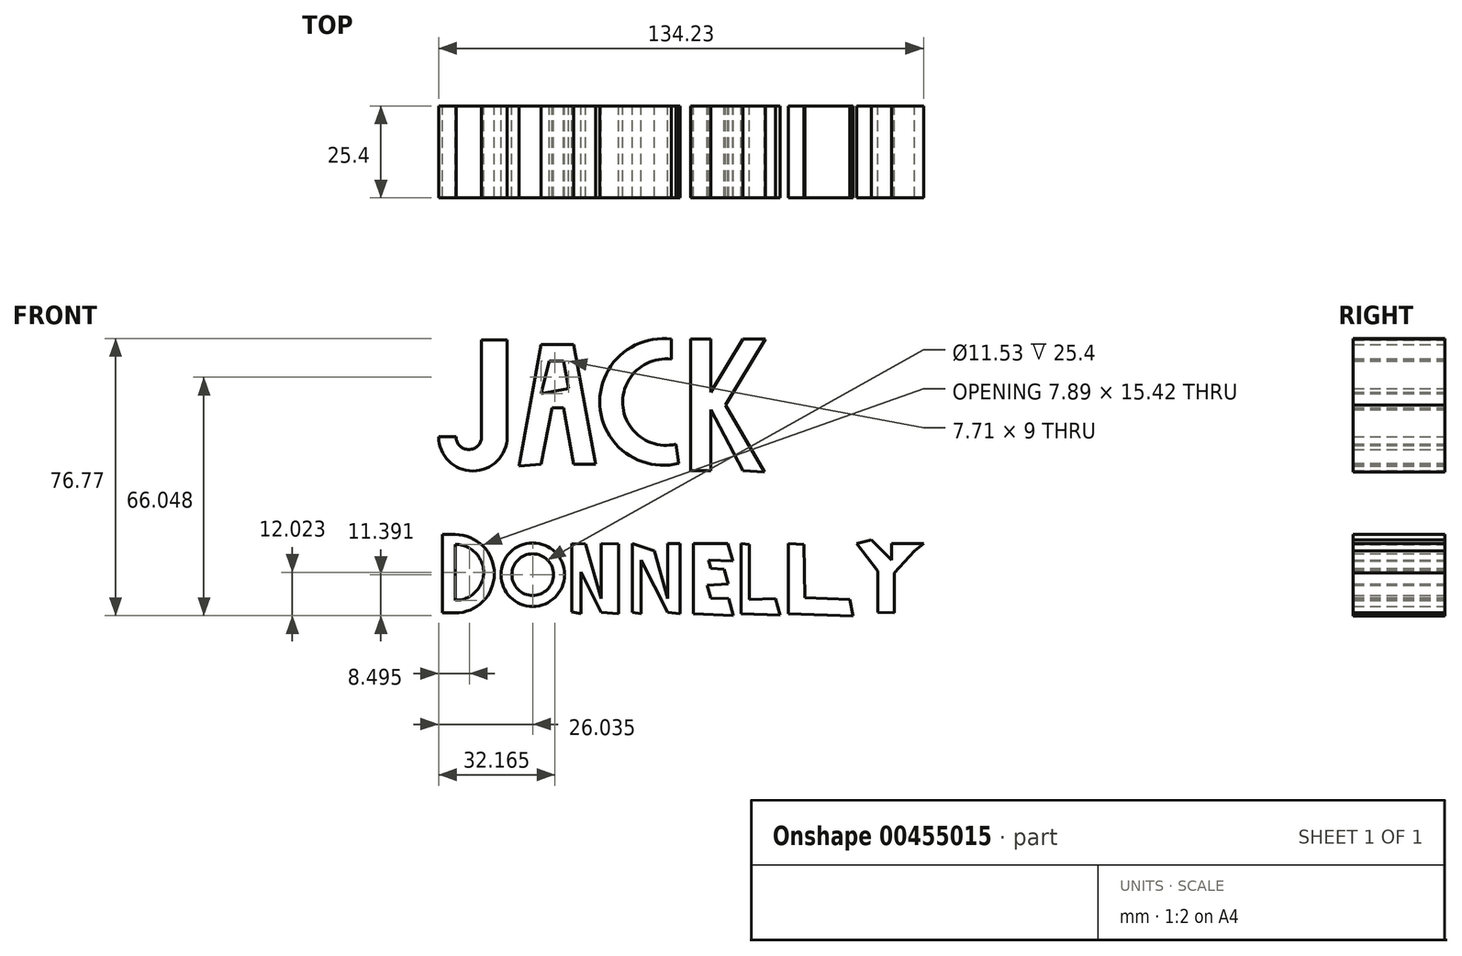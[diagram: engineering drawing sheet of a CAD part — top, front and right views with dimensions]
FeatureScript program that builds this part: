
annotation { "Feature Type Name" : "Feature", "Feature Type Description" : "" }
export const myFeature = defineFeature(function(context is Context, id is Id, definition is map)
    precondition{}
    {
        {
            var Q0;
            Q0=qCreatedBy(makeId("Front.planeOp"),FACE);
            var sketch = newSketch(context, id + "F0", { "sketchPlane" : qUnion([Q0])});
            skLineSegment(sketch, "E0", {"start": v(-63.45, 50.18) * mm, "end": v(-56.37, 50.18) * mm});
            skLineSegment(sketch, "E1", {"start": v(-56.37, 50.18) * mm, "end": v(-56.37, 23.38) * mm});
            skLineSegment(sketch, "E2", {"start": v(-63.45, 50.18) * mm, "end": v(-63.45, 23.38) * mm});
            skArc(sketch, "E3", {"start": v(-75.33, 23.38) * mm, "mid": v(-65.85, 13.9) * mm, "end": v(-56.37, 23.38) * mm});
            skLineSegment(sketch, "E4", {"start": v(-75.33, 23.38) * mm, "end": v(-70.53, 23.38) * mm});
            skArc(sketch, "E5", {"start": v(-70.53, 23.38) * mm, "mid": v(-67, 19.84) * mm, "end": v(-63.45, 23.38) * mm});
            skLineSegment(sketch, "E6", {"start": v(-53.09, 15.3) * mm, "end": v(-47.02, 48.92) * mm});
            skLineSegment(sketch, "E7", {"start": v(-47.02, 48.92) * mm, "end": v(-37.92, 48.92) * mm});
            skLineSegment(sketch, "E8", {"start": v(-37.92, 48.92) * mm, "end": v(-31.85, 15.8) * mm});
            skLineSegment(sketch, "E9", {"start": v(-31.85, 15.8) * mm, "end": v(-37.92, 15.8) * mm});
            skLineSegment(sketch, "E10", {"start": v(-37.92, 15.8) * mm, "end": v(-40.7, 31.47) * mm});
            skLineSegment(sketch, "E11", {"start": v(-40.7, 31.47) * mm, "end": v(-43.99, 31.47) * mm});
            skLineSegment(sketch, "E12", {"start": v(-43.99, 31.47) * mm, "end": v(-47.02, 15.8) * mm});
            skLineSegment(sketch, "E13", {"start": v(-47.02, 15.8) * mm, "end": v(-53.09, 15.3) * mm});
            skLineSegment(sketch, "E14", {"start": v(-44.74, 44.37) * mm, "end": v(-40.7, 44.37) * mm});
            skLineSegment(sketch, "E15", {"start": v(-40.7, 44.37) * mm, "end": v(-39.31, 36.78) * mm});
            skPoint(sketch, "E15.endSnap0", {"position": v(-56.37, 36.78) * mm});
            skLineSegment(sketch, "E16", {"start": v(-39.31, 36.78) * mm, "end": v(-47.02, 35.37) * mm});
            skLineSegment(sketch, "E17", {"start": v(-44.74, 44.37) * mm, "end": v(-47.02, 35.37) * mm});
            skArc(sketch, "E18", {"start": v(-10.87, 50.43) * mm, "mid": v(-30.7, 32.02) * mm, "end": v(-8.85, 16.05) * mm});
            skArc(sketch, "E19", {"start": v(-10.87, 44.87) * mm, "mid": v(-24.36, 32.36) * mm, "end": v(-9.6, 21.36) * mm});
            skLineSegment(sketch, "E20", {"start": v(-10.87, 50.43) * mm, "end": v(-10.87, 44.87) * mm});
            skLineSegment(sketch, "E21", {"start": v(-9.6, 21.36) * mm, "end": v(-8.85, 16.05) * mm});
            skLineSegment(sketch, "E22", {"start": v(-5.56, 50.43) * mm, "end": v(-5.56, 14.03) * mm});
            skLineSegment(sketch, "E23", {"start": v(-5.56, 14.03) * mm, "end": v(0, 14.03) * mm});
            skLineSegment(sketch, "E24", {"start": v(0, 14.03) * mm, "end": v(0, 30.97) * mm});
            skLineSegment(sketch, "E25", {"start": v(0, 30.97) * mm, "end": v(8.85, 14.03) * mm});
            skLineSegment(sketch, "E26", {"start": v(8.85, 14.03) * mm, "end": v(14.9, 13.63) * mm});
            skLineSegment(sketch, "E27", {"start": v(14.9, 13.63) * mm, "end": v(4.04, 32.23) * mm});
            skLineSegment(sketch, "E28", {"start": v(4.04, 32.23) * mm, "end": v(15.17, 50.43) * mm});
            skLineSegment(sketch, "E29", {"start": v(15.17, 50.43) * mm, "end": v(8.85, 50.47) * mm});
            skLineSegment(sketch, "E30", {"start": v(8.85, 50.47) * mm, "end": v(0, 35.77) * mm});
            skLineSegment(sketch, "E31", {"start": v(0, 35.77) * mm, "end": v(0, 50.43) * mm});
            skLineSegment(sketch, "E32", {"start": v(0, 50.43) * mm, "end": v(-5.56, 50.43) * mm});
            skLineSegment(sketch, "E33", {"start": v(-74.32, -3.67) * mm, "end": v(-74.32, -25.4) * mm});
            skLineSegment(sketch, "E34", {"start": v(-74.32, -25.4) * mm, "end": v(-70.78, -25.4) * mm});
            skLineSegment(sketch, "E35", {"start": v(-74.32, -3.67) * mm, "end": v(-70.78, -3.67) * mm});
            skArc(sketch, "E36", {"start": v(-70.78, -25.4) * mm, "mid": v(-59.91, -14.54) * mm, "end": v(-70.78, -3.67) * mm});
            skLineSegment(sketch, "E37", {"start": v(-70.78, -6.45) * mm, "end": v(-70.78, -21.87) * mm});
            skArc(sketch, "E38", {"start": v(-70.78, -21.87) * mm, "mid": v(-62.89, -14.16) * mm, "end": v(-70.78, -6.45) * mm});
            skCircle(sketch, "E39", {"center": v(-49.3, -14.79) * mm, "radius": 8.8 * mm});
            skCircle(sketch, "E40", {"center": v(-49.3, -14.79) * mm, "radius": 5.76 * mm});
            skLineSegment(sketch, "E41", {"start": v(-38.43, -25.15) * mm, "end": v(-38.43, -6.2) * mm});
            skLineSegment(sketch, "E42", {"start": v(-38.43, -6.2) * mm, "end": v(-34.63, -6.26) * mm});
            skLineSegment(sketch, "E43", {"start": v(-34.63, -6.26) * mm, "end": v(-30.34, -21.36) * mm});
            skLineSegment(sketch, "E44", {"start": v(-30.34, -21.36) * mm, "end": v(-30.34, -6.2) * mm});
            skLineSegment(sketch, "E45", {"start": v(-30.34, -6.2) * mm, "end": v(-25.52, -6.24) * mm});
            skLineSegment(sketch, "E46", {"start": v(-25.52, -6.24) * mm, "end": v(-25.52, -25.66) * mm});
            skLineSegment(sketch, "E47", {"start": v(-25.52, -25.66) * mm, "end": v(-30.34, -25.25) * mm});
            skLineSegment(sketch, "E48", {"start": v(-30.34, -25.25) * mm, "end": v(-35.9, -14.03) * mm});
            skLineSegment(sketch, "E49", {"start": v(-35.9, -14.03) * mm, "end": v(-35.9, -25.66) * mm});
            skLineSegment(sketch, "E50", {"start": v(-35.9, -25.66) * mm, "end": v(-38.43, -25.15) * mm});
            skLineSegment(sketch, "E51", {"start": v(-21.74, -6.2) * mm, "end": v(-21.74, -25.25) * mm});
            skLineSegment(sketch, "E52", {"start": v(-21.74, -25.25) * mm, "end": v(-19.27, -25.66) * mm});
            skLineSegment(sketch, "E53", {"start": v(-19.27, -25.66) * mm, "end": v(-19.27, -10.74) * mm});
            skLineSegment(sketch, "E54", {"start": v(-19.27, -10.74) * mm, "end": v(-11.88, -25.25) * mm});
            skLineSegment(sketch, "E55", {"start": v(-11.88, -25.25) * mm, "end": v(-8.55, -25.66) * mm});
            skLineSegment(sketch, "E56", {"start": v(-8.55, -25.66) * mm, "end": v(-8.55, -6.2) * mm});
            skLineSegment(sketch, "E57", {"start": v(-8.55, -6.2) * mm, "end": v(-11.88, -6.18) * mm});
            skLineSegment(sketch, "E58", {"start": v(-11.88, -6.18) * mm, "end": v(-11.88, -21.36) * mm});
            skLineSegment(sketch, "E59", {"start": v(-11.88, -21.36) * mm, "end": v(-15.6, -8.27) * mm});
            skLineSegment(sketch, "E60", {"start": v(-15.6, -8.27) * mm, "end": v(-21.74, -6.2) * mm});
            skLineSegment(sketch, "E61", {"start": v(-4.8, -6.2) * mm, "end": v(-4.8, -25.66) * mm});
            skLineSegment(sketch, "E62", {"start": v(-4.8, -25.66) * mm, "end": v(6.28, -26.17) * mm});
            skLineSegment(sketch, "E63", {"start": v(6.28, -26.17) * mm, "end": v(4.92, -21.36) * mm});
            skLineSegment(sketch, "E64", {"start": v(4.92, -21.36) * mm, "end": v(0, -21.29) * mm});
            skLineSegment(sketch, "E65", {"start": v(0, -21.29) * mm, "end": v(-1, -17.75) * mm});
            skLineSegment(sketch, "E66", {"start": v(-1, -17.75) * mm, "end": v(4.8, -17.32) * mm});
            skLineSegment(sketch, "E67", {"start": v(4.8, -17.32) * mm, "end": v(3.67, -13.34) * mm});
            skLineSegment(sketch, "E68", {"start": v(3.67, -13.34) * mm, "end": v(0, -13.04) * mm});
            skLineSegment(sketch, "E69", {"start": v(0, -13.04) * mm, "end": v(-0.65, -10.74) * mm});
            skLineSegment(sketch, "E70", {"start": v(-0.65, -10.74) * mm, "end": v(6.05, -10.98) * mm});
            skLineSegment(sketch, "E71", {"start": v(6.05, -10.98) * mm, "end": v(4.68, -6.18) * mm});
            skLineSegment(sketch, "E72", {"start": v(4.68, -6.18) * mm, "end": v(-4.8, -6.2) * mm});
            skLineSegment(sketch, "E73", {"start": v(8.34, -6.2) * mm, "end": v(8.34, -25.66) * mm});
            skLineSegment(sketch, "E74", {"start": v(8.34, -25.66) * mm, "end": v(19.2, -26.05) * mm});
            skLineSegment(sketch, "E75", {"start": v(19.2, -26.05) * mm, "end": v(17.87, -21.36) * mm});
            skLineSegment(sketch, "E76", {"start": v(17.87, -21.36) * mm, "end": v(10.62, -21.61) * mm});
            skLineSegment(sketch, "E77", {"start": v(21.49, -6.2) * mm, "end": v(21.49, -25.66) * mm});
            skLineSegment(sketch, "E78", {"start": v(21.49, -25.66) * mm, "end": v(39.4, -26.18) * mm});
            skLineSegment(sketch, "E79", {"start": v(39.4, -26.18) * mm, "end": v(38.43, -21.61) * mm});
            skLineSegment(sketch, "E80", {"start": v(38.43, -21.61) * mm, "end": v(26.04, -21.1) * mm});
            skLineSegment(sketch, "E81", {"start": v(26.04, -21.1) * mm, "end": v(25.79, -6.45) * mm});
            skLineSegment(sketch, "E82", {"start": v(25.79, -6.45) * mm, "end": v(21.49, -6.2) * mm});
            skLineSegment(sketch, "E83", {"start": v(40.45, -6.2) * mm, "end": v(46.26, -13.78) * mm});
            skLineSegment(sketch, "E84", {"start": v(46.26, -13.78) * mm, "end": v(46.26, -25.25) * mm});
            skLineSegment(sketch, "E85", {"start": v(46.26, -25.25) * mm, "end": v(50.8, -25.32) * mm});
            skLineSegment(sketch, "E86", {"start": v(50.8, -25.32) * mm, "end": v(50.8, -14.28) * mm});
            skLineSegment(sketch, "E87", {"start": v(50.8, -14.28) * mm, "end": v(56.37, -8.27) * mm});
            skLineSegment(sketch, "E88", {"start": v(56.37, -8.27) * mm, "end": v(58.9, -6.2) * mm});
            skLineSegment(sketch, "E89", {"start": v(58.9, -6.2) * mm, "end": v(50.05, -6.18) * mm});
            skLineSegment(sketch, "E90", {"start": v(50.05, -6.18) * mm, "end": v(50.05, -10.74) * mm});
            skLineSegment(sketch, "E91", {"start": v(50.05, -10.74) * mm, "end": v(44.5, -5.18) * mm});
            skLineSegment(sketch, "E92", {"start": v(44.5, -5.18) * mm, "end": v(40.45, -6.2) * mm});
            skLineSegment(sketch, "E93", {"start": v(10.62, -21.61) * mm, "end": v(10.62, -6.45) * mm});
            skLineSegment(sketch, "E94", {"start": v(10.62, -6.45) * mm, "end": v(8.34, -6.2) * mm});
            skSolve(sketch);
        }
        {
            var Q0;
            Q0 = qSketchRegion(id + "F0", true);
            extrude(context, id + "F1", {"entities" : qUnion([Q0]), "depth" : 25.4 * mm});
        }
    });
